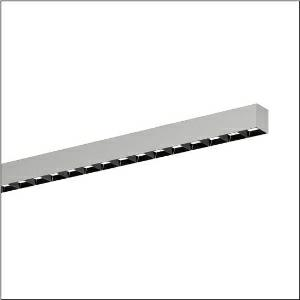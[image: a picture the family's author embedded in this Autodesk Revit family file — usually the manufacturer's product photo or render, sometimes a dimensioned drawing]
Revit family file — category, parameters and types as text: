
# Revit family: silica_r__21_51mx22tat4s_f26d
name_source: partatom
category: Lighting Fixtures
units: mm (PartAtom-declared; Revit-internal decimal feet)

## family parameters
Cut with Voids When Loaded = No
Host = Face
Light Source = No
Part Type = Normal
Room Calculation Point = No
Round Connector Dimension = Use Diameter
Shared = No

## types (1)
- --- (1 x LED, 3720 lm, 32.1 W, 6500K)
    Apparent Load = 32 VA
    CIE Flux Codes = 84 100 100 100 100
    Color Rendering = 80
    Color Temperature = 6500K
    Default Elevation = 1800 mm
    Description = Silica® 21, office luminaire, primary light control with darklight reflector, of PMMA, black, CAT 2 (L<= 3000cd/m²), light emission: direct distribution, primary light characteristic: symmetric, installation type: surface-mounted, LED, rated luminous flux: 3.720lm, luminous efficacy: 110lm/W, light colour: 8tw, colour temperature: 2700..6500K, control gear: DALI DT8, with terminal, 3+2-pole, max. 2.5mm², mains connection: 220..240V, AC, 50/60Hz, rated input power: 33.8W, luminaire housing, of aluminium, metallic grey (RAL 9006), length: 1.204mm, width: 53mm, height: 53mm, protection rating (complete): IP20, insulation class (complete): insulation class I (protective earthing), certification: CE, permissible operating ambient temperature: 0..+35°C, standard: EN 50419, packaging unit: 1 piece
    Height = 53 mm
    Lamp = 1 x LED
    Lamp Light Flux = 3720 lm
    Lamp Power = 32.1 W
    Lamp count = 1
    Length = 1204 mm
    Luminous efficacy = 116 lm/W
    Manufacturer = Siteco
    ModVariant = No
    Model = 51MX22TAT4S
    Mounting Place = Ceiling
    Mounting Type = Surface mounted
    Number of Poles = 1
    OnlyDefault = Yes
    Power Factor = 1
    Product Name = Silica® 21
    Product group = office luminaire | ceiling mounted
    ProductGroupID = 302
    Protection Class = Protection class I
    Protection Degree = IP 20
    RLX_Detail_Level = 1
    RLX_Emergency_Light_Flux = 0 lm
    RLX_Emergency_Type = 0
    RLX_Emergency_Type_DB = No
    RlxData = <blob elided: 39409 chars, md5=01a7d421>
    Socket = socket
    Standby Power = 0 W
    System Light Flux = 3720 lm
    System Power = 32 W
    Type Comments = individual setting
    Type Image = l_1335929.jpg
    URL = http://relux.com
    VarID = @adj_140124
    Voltage = 0 V
    Weight = 0.00 kg
    Width = 53 mm

## geometry (parser evidence)
native form markers: Blend x4, Sweep x11
no freeform markers — native parametric forms only
